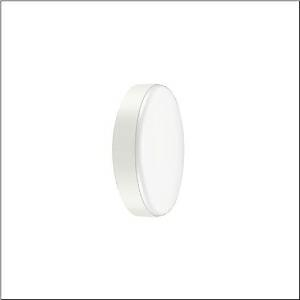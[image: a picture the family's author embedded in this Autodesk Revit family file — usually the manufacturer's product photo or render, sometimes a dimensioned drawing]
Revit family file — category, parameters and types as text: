
# Revit family: rondel_31_51wc10da42as
name_source: partatom
category: Lighting Fixtures
units: mm (PartAtom-declared; Revit-internal decimal feet)

## family parameters
Cut with Voids When Loaded = No
Host = Face
Light Source = No
Part Type = Normal
Room Calculation Point = No
Round Connector Dimension = Use Diameter
Shared = No

## types (1)
- Rondel 31 (1 x LED, 2550 lm, 20.5 W, 4000K)
    Apparent Load = 21 VA
    CIE Flux Codes = 44 75 94 94 100
    Color Rendering = 80
    Color Temperature = 4000K
    Default Elevation = 1800 mm
    Description = Rondel 31, wall and ceiling luminaire, primary optical cover: cover, of PC, opal, light emission: direct distribution, primary light characteristic: symmetric, installation type: surface-mounted, LED, rated luminous flux: 2.400lm, luminous efficacy: 117lm/W, light colour: 840, colour temperature: 4000K, with terminal, 5-pole, max. 2.5mm², mains connection: 220..240V, AC, 50/60Hz, rated input power: 20.5W, luminaire housing, of PC, traffic white (RAL 9016), diameter: 350mm, brightness and presence sensor, HF sensor, protection rating (complete): IP65, insulation class (complete): insulation class II (safety insulation), certification: CE, impact resistance: IK10, permissible storage temperature: -20..+60°C, packaging unit: 1 piece
    Height = 97 mm
    Lamp = 1 x LED
    Lamp Light Flux = 2550 lm
    Lamp Power = 20.5 W
    Lamp count = 1
    Length = 350 mm
    Luminous efficacy = 124 lm/W
    Manufacturer = Siteco
    ModVariant = No
    Model = 51WC10DA42AS
    Mounting Place = Ceiling
    Mounting Type = Surface mounted
    Number of Poles = 1
    OnlyDefault = Yes
    Power Factor = 1
    Product Name = Rondel 31
    Product group = wall and ceiling luminaire
    ProductGroupID = 301
    Protection Class = Protection class II
    Protection Degree = IP 65
    RLX_Detail_Level = 1
    RlxData = <blob elided: 29461 chars, md5=b8dcecf3>
    Socket = socket
    Standby Power = 0 W
    System Light Flux = 2550 lm
    System Power = 21 W
    Type Comments = Product without accessories
    Type Image = l_1007027.jpg
    URL = http://relux.com
    VarID = ---
    Voltage = 0 V
    Weight = 0.00 kg
    Width = 0 mm  [stored 0 ft]

note: [stored X ft] marks values corroborated as IEEE doubles in the binary element streams (Revit-internal decimal feet)

## geometry (parser evidence)
native form markers: Blend x4, Sweep x13
no freeform markers — native parametric forms only
